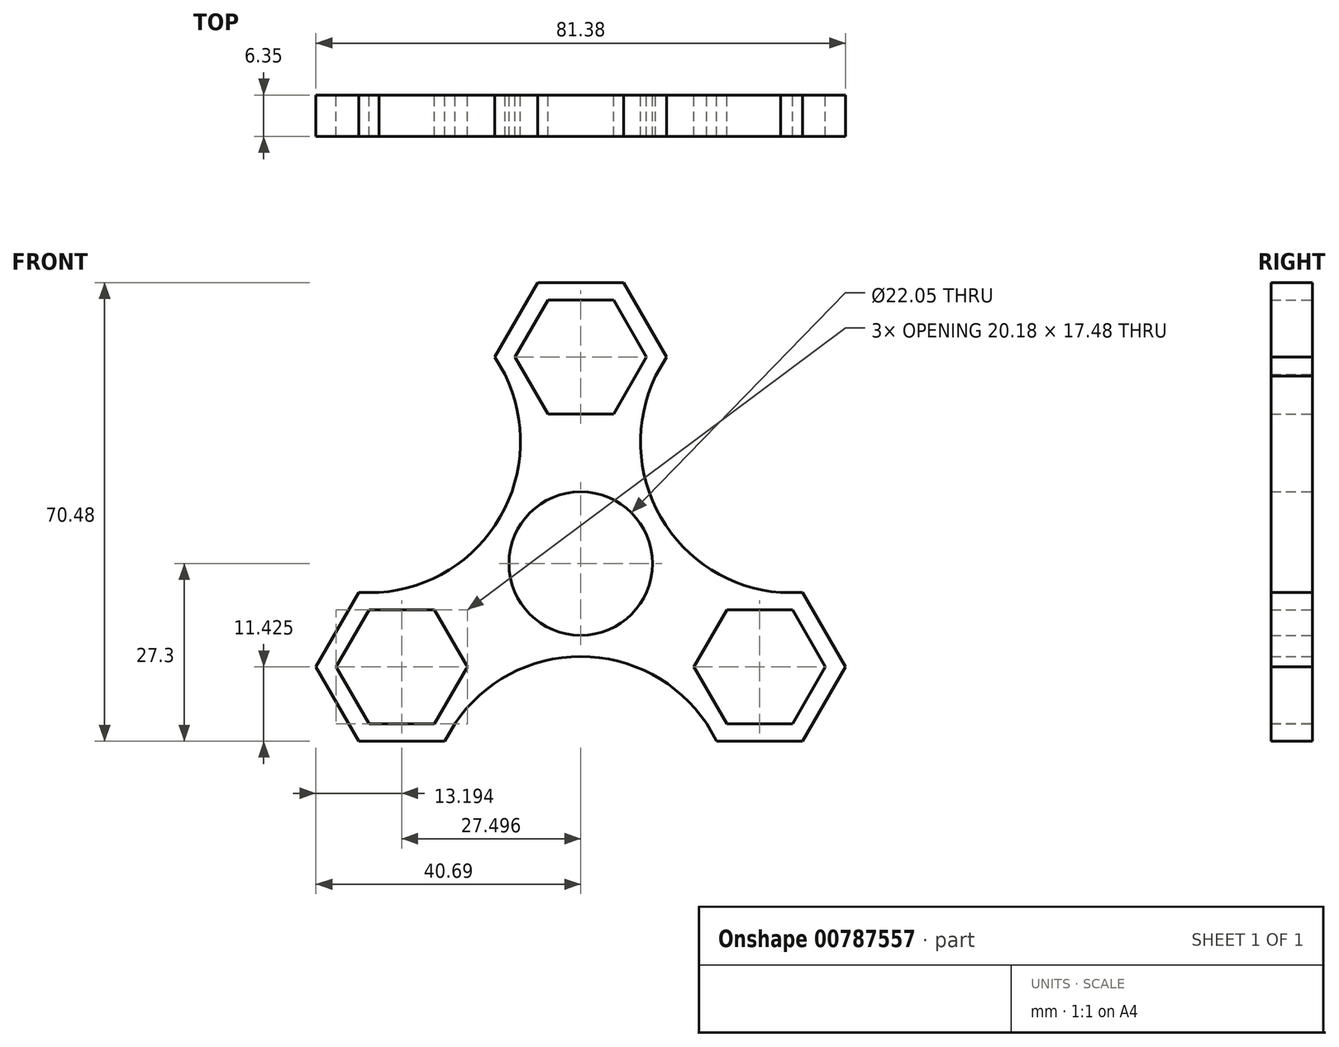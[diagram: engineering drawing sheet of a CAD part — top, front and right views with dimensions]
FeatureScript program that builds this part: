
annotation { "Feature Type Name" : "Feature", "Feature Type Description" : "" }
export const myFeature = defineFeature(function(context is Context, id is Id, definition is map)
    precondition{}
    {
        {
            var Q0;
            Q0=qCreatedBy(makeId("Front.planeOp"),FACE);
            var sketch = newSketch(context, id + "F0", { "sketchPlane" : qUnion([Q0])});
            skCircle(sketch, "E0", {"center": v(0, 0) * mm, "radius": 11.02 * mm});
            skCircle(sketch, "E1", {"center": v(0, 0) * mm, "radius": 14.29 * mm});
            skCircle(sketch, "E2.cCircle", {"center": v(0, 31.75) * mm, "radius": 8.74 * mm, "construction": true});
            skLineSegment(sketch, "E2.0", {"start": v(5.04, 23.01) * mm, "end": v(-5.04, 23.01) * mm});
            skLineSegment(sketch, "E2.1", {"start": v(-5.04, 23.01) * mm, "end": v(-10.09, 31.75) * mm});
            skLineSegment(sketch, "E2.2", {"start": v(-10.09, 31.75) * mm, "end": v(-5.04, 40.49) * mm});
            skLineSegment(sketch, "E2.3", {"start": v(-5.04, 40.49) * mm, "end": v(5.04, 40.49) * mm});
            skLineSegment(sketch, "E2.4", {"start": v(5.04, 40.49) * mm, "end": v(10.09, 31.75) * mm});
            skLineSegment(sketch, "E2.5", {"start": v(10.09, 31.75) * mm, "end": v(5.04, 23.01) * mm});
            skPoint(sketch, "E2.0.midPoint", {"position": v(0, 23.01) * mm});
            skCircle(sketch, "E3.cCircle", {"center": v(0, 31.75) * mm, "radius": 11.43 * mm, "construction": true});
            skLineSegment(sketch, "E3.0", {"start": v(13.2, 31.75) * mm, "end": v(6.6, 20.32) * mm});
            skLineSegment(sketch, "E3.1", {"start": v(6.6, 20.32) * mm, "end": v(-6.6, 20.32) * mm});
            skLineSegment(sketch, "E3.2", {"start": v(-6.6, 20.32) * mm, "end": v(-13.2, 31.75) * mm});
            skLineSegment(sketch, "E3.3", {"start": v(-13.2, 31.75) * mm, "end": v(-6.6, 43.18) * mm});
            skLineSegment(sketch, "E3.4", {"start": v(-6.6, 43.18) * mm, "end": v(6.6, 43.18) * mm});
            skLineSegment(sketch, "E3.5", {"start": v(6.6, 43.18) * mm, "end": v(13.2, 31.75) * mm});
            skPoint(sketch, "E3.0.midPoint", {"position": v(9.9, 26.04) * mm});
            skLineSegment(sketch, "E4.1.0", {"start": v(-32.54, -24.61) * mm, "end": v(-37.59, -15.87) * mm});
            skLineSegment(sketch, "E4.1.1", {"start": v(-22.45, -24.61) * mm, "end": v(-32.54, -24.61) * mm});
            skLineSegment(sketch, "E4.1.2", {"start": v(-17.4, -15.87) * mm, "end": v(-22.45, -24.61) * mm});
            skLineSegment(sketch, "E4.1.3", {"start": v(-22.45, -7.14) * mm, "end": v(-17.4, -15.87) * mm});
            skLineSegment(sketch, "E4.1.4", {"start": v(-32.54, -7.14) * mm, "end": v(-22.45, -7.14) * mm});
            skLineSegment(sketch, "E4.1.5", {"start": v(-37.59, -15.87) * mm, "end": v(-32.54, -7.14) * mm});
            skCircle(sketch, "E4.1.6", {"center": v(-27.5, -15.87) * mm, "radius": 8.74 * mm, "construction": true});
            skCircle(sketch, "E4.1.7", {"center": v(-27.5, -15.87) * mm, "radius": 11.43 * mm, "construction": true});
            skLineSegment(sketch, "E4.1.8", {"start": v(-20.9, -27.3) * mm, "end": v(-34.1, -27.3) * mm});
            skLineSegment(sketch, "E4.1.9", {"start": v(-14.3, -15.87) * mm, "end": v(-20.9, -27.3) * mm});
            skLineSegment(sketch, "E4.1.10", {"start": v(-20.9, -4.44) * mm, "end": v(-14.3, -15.88) * mm});
            skLineSegment(sketch, "E4.1.11", {"start": v(-34.1, -4.44) * mm, "end": v(-20.9, -4.44) * mm});
            skLineSegment(sketch, "E4.1.12", {"start": v(-40.7, -15.87) * mm, "end": v(-34.1, -4.44) * mm});
            skLineSegment(sketch, "E4.1.13", {"start": v(-34.1, -27.3) * mm, "end": v(-40.7, -15.87) * mm});
            skLineSegment(sketch, "E4.2.0", {"start": v(37.59, -15.88) * mm, "end": v(32.54, -24.61) * mm});
            skLineSegment(sketch, "E4.2.1", {"start": v(32.54, -7.14) * mm, "end": v(37.59, -15.88) * mm});
            skLineSegment(sketch, "E4.2.2", {"start": v(22.45, -7.14) * mm, "end": v(32.54, -7.14) * mm});
            skLineSegment(sketch, "E4.2.3", {"start": v(17.4, -15.88) * mm, "end": v(22.45, -7.14) * mm});
            skLineSegment(sketch, "E4.2.4", {"start": v(22.45, -24.61) * mm, "end": v(17.4, -15.88) * mm});
            skLineSegment(sketch, "E4.2.5", {"start": v(32.54, -24.61) * mm, "end": v(22.45, -24.61) * mm});
            skCircle(sketch, "E4.2.6", {"center": v(27.5, -15.88) * mm, "radius": 8.74 * mm, "construction": true});
            skCircle(sketch, "E4.2.7", {"center": v(27.5, -15.88) * mm, "radius": 11.43 * mm, "construction": true});
            skLineSegment(sketch, "E4.2.8", {"start": v(34.1, -4.45) * mm, "end": v(40.7, -15.88) * mm});
            skLineSegment(sketch, "E4.2.9", {"start": v(20.9, -4.45) * mm, "end": v(34.1, -4.45) * mm});
            skLineSegment(sketch, "E4.2.10", {"start": v(14.3, -15.88) * mm, "end": v(20.9, -4.45) * mm});
            skLineSegment(sketch, "E4.2.11", {"start": v(20.9, -27.3) * mm, "end": v(14.3, -15.88) * mm});
            skLineSegment(sketch, "E4.2.12", {"start": v(34.1, -27.3) * mm, "end": v(20.9, -27.3) * mm});
            skLineSegment(sketch, "E4.2.13", {"start": v(40.7, -15.88) * mm, "end": v(34.1, -27.3) * mm});
            skArc(sketch, "E5", {"start": v(-34.1, -4.44) * mm, "mid": v(-12.37, 7.14) * mm, "end": v(-13.2, 31.75) * mm});
            skArc(sketch, "E6", {"start": v(20.9, -27.3) * mm, "mid": v(0, -14.29) * mm, "end": v(-20.9, -27.3) * mm});
            skArc(sketch, "E7", {"start": v(13.2, 31.75) * mm, "mid": v(12.3, 7.1) * mm, "end": v(34.1, -4.45) * mm});
            skSolve(sketch);
        }
        {
            var Q0;
            {var subQ0=sQuery(id+"F0.wireOp",EDGE,"E7");var subQ1=sQuery(id+"F0.wireOp",EDGE,"E1");var subQ2=makeQuery(id+"F0.imprint","INTERSECT",VERTEX,{"disambiguationData":[OD(0.0)],"derivedFrom":[subQ1,subQ0]});Q0=makeQuery(id+"F0.imprint","IMPRINT",FACE,{"disambiguationData":[TD([[makeQuery(id+"F0.imprint","IMPRINT",EDGE,{"disambiguationData":[TD([[subQ2,1.0]])],"derivedFrom":subQ1}),1.0]])]});}
            var Q1;
            {var subQ0=sQuery(id+"F0.wireOp",EDGE,"E6");var subQ1=sQuery(id+"F0.wireOp",EDGE,"E1");var subQ2=makeQuery(id+"F0.imprint","INTERSECT",VERTEX,{"disambiguationData":[OD(0.0)],"derivedFrom":[subQ1,subQ0]});Q1=makeQuery(id+"F0.imprint","IMPRINT",FACE,{"disambiguationData":[TD([[makeQuery(id+"F0.imprint","IMPRINT",EDGE,{"disambiguationData":[TD([[subQ2,-1.0]])],"derivedFrom":subQ1}),1.0]])]});}
            var Q2;
            {var subQ0=sQuery(id+"F0.wireOp",EDGE,"E7");var subQ1=sQuery(id+"F0.wireOp",EDGE,"E3.0");var subQ3=makeQuery(id+"F0.imprint","INTERSECT",VERTEX,{"derivedFrom":[subQ1,subQ0]});Q2=makeQuery(id+"F0.imprint","IMPRINT",FACE,{"disambiguationData":[TD([[makeQuery(id+"F0.imprint","IMPRINT",EDGE,{"disambiguationData":[TD([[subQ3,1.0]])],"derivedFrom":subQ1}),-1.0]])]});}
            var Q3;
            {var subQ0=sQuery(id+"F0.wireOp",EDGE,"E5");var subQ1=sQuery(id+"F0.wireOp",EDGE,"E3.2");var subQ3=makeQuery(id+"F0.imprint","INTERSECT",VERTEX,{"derivedFrom":[subQ1,subQ0]});Q3=makeQuery(id+"F0.imprint","IMPRINT",FACE,{"disambiguationData":[TD([[makeQuery(id+"F0.imprint","IMPRINT",EDGE,{"disambiguationData":[TD([[subQ3,-1.0]])],"derivedFrom":subQ1}),-1.0]])]});}
            var Q4;
            {var subQ0=sQuery(id+"F0.wireOp",EDGE,"E6");var subQ1=sQuery(id+"F0.wireOp",EDGE,"E4.1.9");var subQ3=makeQuery(id+"F0.imprint","INTERSECT",VERTEX,{"derivedFrom":[subQ1,subQ0]});Q4=makeQuery(id+"F0.imprint","IMPRINT",FACE,{"disambiguationData":[TD([[makeQuery(id+"F0.imprint","IMPRINT",EDGE,{"disambiguationData":[TD([[subQ3,-1.0]])],"derivedFrom":subQ1}),-1.0]])]});}
            var Q5;
            {var subQ0=sQuery(id+"F0.wireOp",EDGE,"E5");var subQ1=sQuery(id+"F0.wireOp",EDGE,"E4.1.11");var subQ3=makeQuery(id+"F0.imprint","INTERSECT",VERTEX,{"derivedFrom":[subQ1,subQ0]});Q5=makeQuery(id+"F0.imprint","IMPRINT",FACE,{"disambiguationData":[TD([[makeQuery(id+"F0.imprint","IMPRINT",EDGE,{"disambiguationData":[TD([[subQ3,1.0]])],"derivedFrom":subQ1}),-1.0]])]});}
            var Q6;
            {var subQ0=sQuery(id+"F0.wireOp",EDGE,"E7");var subQ1=sQuery(id+"F0.wireOp",EDGE,"E4.2.9");var subQ3=makeQuery(id+"F0.imprint","INTERSECT",VERTEX,{"derivedFrom":[subQ1,subQ0]});Q6=makeQuery(id+"F0.imprint","IMPRINT",FACE,{"disambiguationData":[TD([[makeQuery(id+"F0.imprint","IMPRINT",EDGE,{"disambiguationData":[TD([[subQ3,-1.0]])],"derivedFrom":subQ1}),-1.0]])]});}
            var Q7;
            {var subQ0=sQuery(id+"F0.wireOp",EDGE,"E6");var subQ1=sQuery(id+"F0.wireOp",EDGE,"E4.2.11");var subQ3=makeQuery(id+"F0.imprint","INTERSECT",VERTEX,{"derivedFrom":[subQ1,subQ0]});Q7=makeQuery(id+"F0.imprint","IMPRINT",FACE,{"disambiguationData":[TD([[makeQuery(id+"F0.imprint","IMPRINT",EDGE,{"disambiguationData":[TD([[subQ3,1.0]])],"derivedFrom":subQ1}),-1.0]])]});}
            var Q8;
            {var subQ0=sQuery(id+"F0.wireOp",EDGE,"E4.2.10");Q8=makeQuery(id+"F0.imprint","IMPRINT",FACE,{"disambiguationData":[TD([[makeQuery(id+"F0.imprint","IMPRINT",EDGE,{"derivedFrom":subQ0}),1.0]])]});}
            var Q9;
            {var subQ1=sQuery(id+"F0.wireOp",EDGE,"E3.1");Q9=makeQuery(id+"F0.imprint","IMPRINT",FACE,{"disambiguationData":[TD([[makeQuery(id+"F0.imprint","IMPRINT",EDGE,{"derivedFrom":subQ1}),1.0]])]});}
            var Q10;
            Q10=makeQuery(id+"F0.imprint","IMPRINT",FACE,{"disambiguationData":[TD([[makeQuery(id+"F0.imprint","IMPRINT",EDGE,{"derivedFrom":sQuery(id+"F0.wireOp",EDGE,"E4.1.0")}),1.0]])]});
            var Q11;
            Q11=makeQuery(id+"F0.imprint","IMPRINT",FACE,{"disambiguationData":[TD([[makeQuery(id+"F0.imprint","IMPRINT",EDGE,{"derivedFrom":sQuery(id+"F0.wireOp",EDGE,"E4.2.0")}),1.0]])]});
            var Q12;
            Q12=makeQuery(id+"F0.imprint","IMPRINT",FACE,{"disambiguationData":[TD([[makeQuery(id+"F0.imprint","IMPRINT",EDGE,{"derivedFrom":sQuery(id+"F0.wireOp",EDGE,"E0")}),-1.0]])]});
            var Q13;
            Q13=makeQuery(id+"F0.imprint","IMPRINT",FACE,{"disambiguationData":[TD([[makeQuery(id+"F0.imprint","IMPRINT",EDGE,{"derivedFrom":sQuery(id+"F0.wireOp",EDGE,"E2.0")}),1.0]])]});
            extrude(context, id + "F1", {"entities" : qUnion([Q0, Q1, Q2, Q3, Q4, Q5, Q6, Q7, Q8, Q9, Q10, Q11, Q12, Q13]), "depth" : 6.35 * mm, "offsetDistance" : 25.4 * mm});
        }
    });
